# Revit family: Haworth_Cappellini_Hi-Pad_Chair_AP_PRELIMINARY
name_source: partatom
category: Furniture
revit_build: Autodesk Revit 2018 (Build: 20170223_1515(x64)
units: mm (PartAtom-declared; Revit-internal decimal feet)

## family parameters
Always vertical = Yes
Cut with Voids When Loaded = No
OmniClass Number = 23.40.70.14.64.21
OmniClass Title = Systems Furniture
Room Calculation Point = No
Shared = No
Work Plane-Based = No

## types (1)
- Chair
    Actual Depth = 525 mm
    Actual Height = 810 mm
    Actual Width = 420 mm  [stored 1.37795 ft]
    Assembly Code = E2020200
    Bar Height = 302 mm
    Bar Position Width = 318 mm
    Base Depth Bottom = 457 mm
    Base Depth Top = 330 mm
    Base Width Bottom = 406 mm
    Base Width Top = 279 mm
    Description = Haworth - Cappellini - Hi-Pad - Chair
    Glide Finish = Haworth _ Polymer _ Black
    Manufacturer = Haworth
    Model = HP_1
    Revision Number = 1
    Size = Verify Final Dim. w/ Haworth
    Top Frame Back = 381 mm
    Top Frame Front = 419 mm
    URL = https://www.haworth.com
    URL - Product = https://www.haworth.com
    Warranty = http://www.haworth.com

note: [stored X ft] marks values corroborated as IEEE doubles in the binary element streams (Revit-internal decimal feet)

## geometry (parser evidence)
native form markers: Blend x6, Sweep x6
no freeform markers — native parametric forms only
